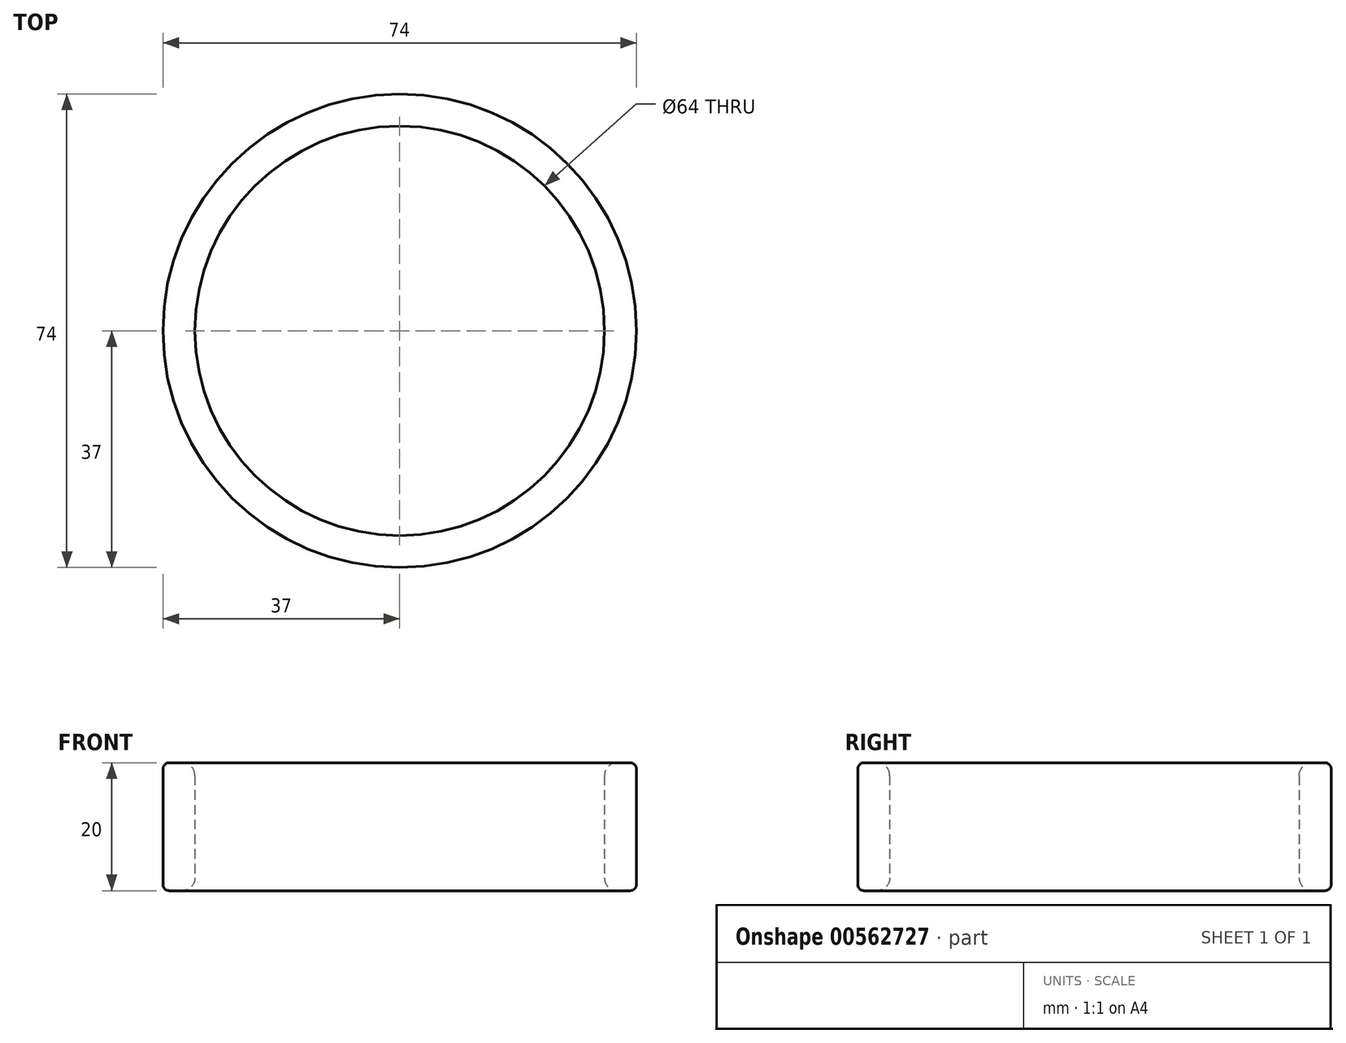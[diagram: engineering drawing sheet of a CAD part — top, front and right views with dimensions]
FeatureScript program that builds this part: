
annotation { "Feature Type Name" : "Feature", "Feature Type Description" : "" }
export const myFeature = defineFeature(function(context is Context, id is Id, definition is map)
    precondition{}
    {
        {
            var Q0;
            Q0=qCreatedBy(makeId("Top.planeOp"),FACE);
            var sketch = newSketch(context, id + "F0", { "sketchPlane" : qUnion([Q0])});
            skCircle(sketch, "E0", {"center": v(0, 0) * mm, "radius": 32 * mm});
            skCircle(sketch, "E1", {"center": v(0, 0) * mm, "radius": 37 * mm});
            skSolve(sketch);
        }
        {
            var Q0;
            Q0 = qSketchRegion(id + "F0", true);
            extrude(context, id + "F1", {"entities" : qUnion([Q0]), "depth" : 20 * mm, "offsetDistance" : 25 * mm});
        }
        {
            var Q0;
            Q0=makeQuery(id+"F1.opExtrude","CAP_EDGE",EDGE,{"disambiguationData":[OSD([sQuery(id+"F0.wireOp",EDGE,"E0")])],"isStart":false});
            var Q1;
            Q1=makeQuery(id+"F1.opExtrude","CAP_EDGE",EDGE,{"disambiguationData":[OSD([sQuery(id+"F0.wireOp",EDGE,"E0")])],"isStart":true});
            fillet(context, id + "F2", {"entities" : qUnion([Q0, Q1]), "radius" : 2 * mm, "tangentPropagation" : true, "allowEdgeOverflow" : false});
        }
        {
            var Q0;
            Q0=makeQuery(id+"F1.opExtrude","CAP_EDGE",EDGE,{"disambiguationData":[OSD([sQuery(id+"F0.wireOp",EDGE,"E1")])],"isStart":false});
            var Q1;
            Q1=makeQuery(id+"F1.opExtrude","CAP_EDGE",EDGE,{"disambiguationData":[OSD([sQuery(id+"F0.wireOp",EDGE,"E1")])],"isStart":true});
            fillet(context, id + "F3", {"entities" : qUnion([Q0, Q1]), "radius" : 1 * mm, "tangentPropagation" : true, "allowEdgeOverflow" : false});
        }
    });
